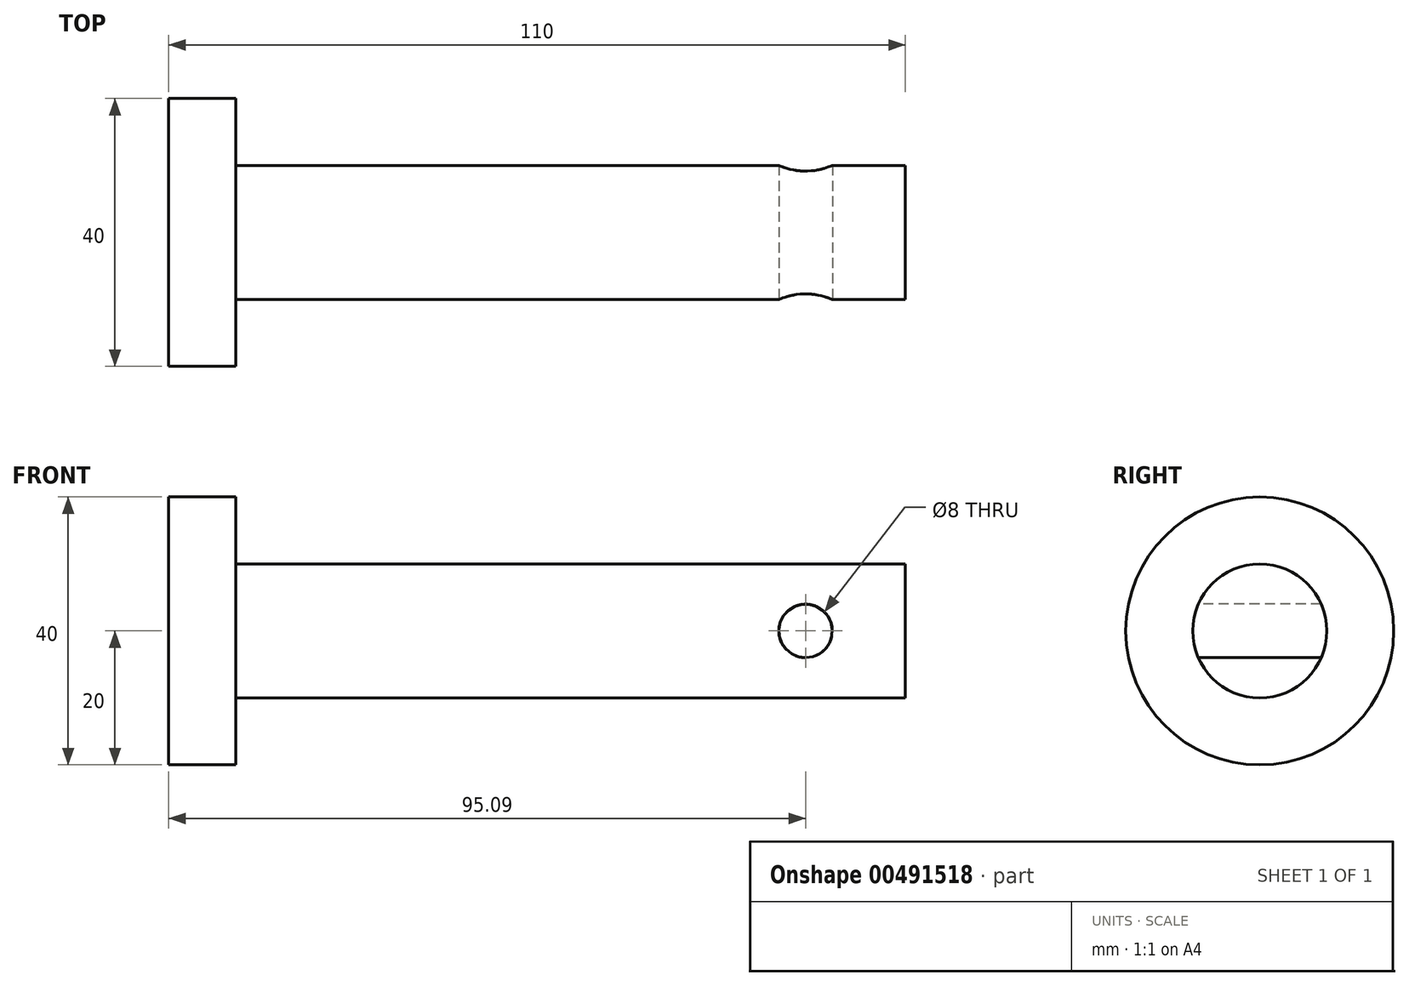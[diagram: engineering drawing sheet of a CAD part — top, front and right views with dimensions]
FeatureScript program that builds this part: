
annotation { "Feature Type Name" : "Feature", "Feature Type Description" : "" }
export const myFeature = defineFeature(function(context is Context, id is Id, definition is map)
    precondition{}
    {
        {
            var Q0;
            Q0=qCreatedBy(makeId("Front.planeOp"),FACE);
            var sketch = newSketch(context, id + "F0", { "sketchPlane" : qUnion([Q0])});
            skLineSegment(sketch, "E0", {"start": v(-75.09, 0) * mm, "end": v(-75.09, 20) * mm});
            skLineSegment(sketch, "E1", {"start": v(-75.09, 20) * mm, "end": v(-65.09, 20) * mm});
            skLineSegment(sketch, "E2", {"start": v(-65.09, 20) * mm, "end": v(-65.09, 10) * mm});
            skLineSegment(sketch, "E3", {"start": v(-65.09, 10) * mm, "end": v(34.91, 10) * mm});
            skLineSegment(sketch, "E4", {"start": v(34.91, 10) * mm, "end": v(34.91, 0) * mm});
            skLineSegment(sketch, "E5", {"start": v(34.91, 0) * mm, "end": v(-75.09, 0) * mm});
            skSolve(sketch);
        }
        {
            var Q0;
            Q0=makeQuery(id+"F0.imprint","IMPRINT",FACE,{"disambiguationData":[TD([[makeQuery(id+"F0.imprint","IMPRINT",EDGE,{"derivedFrom":sQuery(id+"F0.wireOp",EDGE,"E0")}),-1.0]])]});
            var Q1;
            Q1=sQuery(id+"F0.wireOp",EDGE,"E5");
            revolve(context, id + "F1", {"entities" : qUnion([Q0]), "axis" : qUnion([Q1]), "revolveType" : RevolveType.FULL});
        }
        {
            var Q0;
            Q0=qCreatedBy(makeId("Front.planeOp"),FACE);
            var sketch = newSketch(context, id + "F2", { "sketchPlane" : qUnion([Q0])});
            skCircle(sketch, "E6", {"center": v(20, 0) * mm, "radius": 4 * mm});
            skSolve(sketch);
        }
        {
            var Q0;
            Q0=qSketchRegion(id+"F2",true);
            var Q1;
            Q1=sQuery(id+"F2.wireOp",EDGE,"E6");
            extrude(context, id + "F3", {"entities" : qUnion([Q0]), "operationType" : NewBodyOperationType.REMOVE, "surfaceEntities" : qUnion([Q1]), "endBound" : BoundingType.SYMMETRIC, "oppositeDirection" : true, "depth" : 100 * mm});
        }
    });
